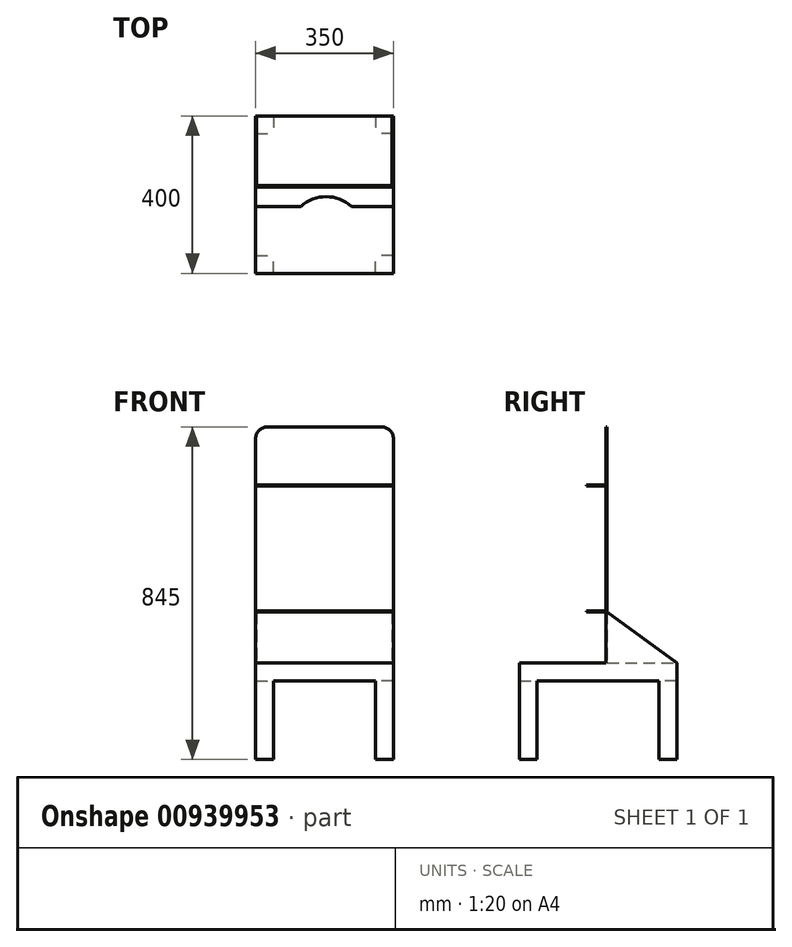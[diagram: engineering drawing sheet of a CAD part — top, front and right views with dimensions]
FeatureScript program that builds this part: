
annotation { "Feature Type Name" : "Feature", "Feature Type Description" : "" }
export const myFeature = defineFeature(function(context is Context, id is Id, definition is map)
    precondition{}
    {
        {
            var Q0;
            Q0=qCreatedBy(makeId("Top.planeOp"),FACE);
            var sketch = newSketch(context, id + "F0", { "sketchPlane" : qUnion([Q0])});
            skLineSegment(sketch, "E0.bottom", {"start": v(175, -200) * mm, "end": v(-175, -200) * mm});
            skLineSegment(sketch, "E0.top", {"start": v(175, 200) * mm, "end": v(-175, 200) * mm});
            skLineSegment(sketch, "E0.left", {"start": v(175, -200) * mm, "end": v(175, 200) * mm});
            skLineSegment(sketch, "E0.right", {"start": v(-175, -200) * mm, "end": v(-175, 200) * mm});
            skPoint(sketch, "E0.middle", {"position": v(0, 0) * mm});
            skSolve(sketch);
        }
        {
            var Q0;
            Q0=makeQuery(id+"F0.imprint","IMPRINT",FACE,{"disambiguationData":[TD([[makeQuery(id+"F0.imprint","IMPRINT",EDGE,{"derivedFrom":sQuery(id+"F0.wireOp",EDGE,"E0.bottom")}),-1.0]])]});
            extrude(context, id + "F1", {"entities" : qUnion([Q0]), "depth" : 45 * mm, "offsetDistance" : 25 * mm});
        }
        {
            var Q0;
            Q0=makeQuery(id+"F1.opExtrude","CAP_FACE",FACE,{"disambiguationData":[OSD([sQuery(id+"F0.wireOp",EDGE,"E0.bottom"),sQuery(id+"F0.wireOp",EDGE,"E0.top"),sQuery(id+"F0.wireOp",EDGE,"E0.left"),sQuery(id+"F0.wireOp",EDGE,"E0.right")])],"isStart":true});
            var sketch = newSketch(context, id + "F2", { "sketchPlane" : qUnion([Q0])});
            skLineSegment(sketch, "E1.bottom", {"start": v(-175, 200) * mm, "end": v(-130, 200) * mm});
            skLineSegment(sketch, "E1.top", {"start": v(-175, 155) * mm, "end": v(-130, 155) * mm});
            skLineSegment(sketch, "E1.left", {"start": v(-175, 200) * mm, "end": v(-175, 155) * mm});
            skLineSegment(sketch, "E1.right", {"start": v(-130, 200) * mm, "end": v(-130, 155) * mm});
            skLineSegment(sketch, "E2.bottom", {"start": v(175, 200) * mm, "end": v(130, 200) * mm});
            skLineSegment(sketch, "E2.top", {"start": v(175, 155) * mm, "end": v(130, 155) * mm});
            skLineSegment(sketch, "E2.left", {"start": v(175, 200) * mm, "end": v(175, 155) * mm});
            skLineSegment(sketch, "E2.right", {"start": v(130, 200) * mm, "end": v(130, 155) * mm});
            skLineSegment(sketch, "E3.bottom", {"start": v(-175, -200) * mm, "end": v(-130, -200) * mm});
            skLineSegment(sketch, "E3.top", {"start": v(-175, -155) * mm, "end": v(-130, -155) * mm});
            skLineSegment(sketch, "E3.left", {"start": v(-175, -200) * mm, "end": v(-175, -155) * mm});
            skLineSegment(sketch, "E3.right", {"start": v(-130, -200) * mm, "end": v(-130, -155) * mm});
            skLineSegment(sketch, "E4.bottom", {"start": v(175, -200) * mm, "end": v(130, -200) * mm});
            skLineSegment(sketch, "E4.top", {"start": v(175, -155) * mm, "end": v(130, -155) * mm});
            skLineSegment(sketch, "E4.left", {"start": v(175, -200) * mm, "end": v(175, -155) * mm});
            skLineSegment(sketch, "E4.right", {"start": v(130, -200) * mm, "end": v(130, -155) * mm});
            skSolve(sketch);
        }
        {
            var Q0;
            Q0=makeQuery(id+"F2.imprint","IMPRINT",FACE,{"disambiguationData":[TD([[makeQuery(id+"F2.imprint","IMPRINT",EDGE,{"derivedFrom":sQuery(id+"F2.wireOp",EDGE,"E1.bottom")}),1.0]])]});
            var Q1;
            Q1=makeQuery(id+"F2.imprint","IMPRINT",FACE,{"disambiguationData":[TD([[makeQuery(id+"F2.imprint","IMPRINT",EDGE,{"derivedFrom":sQuery(id+"F2.wireOp",EDGE,"E2.bottom")}),1.0]])]});
            var Q2;
            Q2=makeQuery(id+"F2.imprint","IMPRINT",FACE,{"disambiguationData":[TD([[makeQuery(id+"F2.imprint","IMPRINT",EDGE,{"derivedFrom":sQuery(id+"F2.wireOp",EDGE,"E3.bottom")}),-1.0]])]});
            var Q3;
            Q3=makeQuery(id+"F2.imprint","IMPRINT",FACE,{"disambiguationData":[TD([[makeQuery(id+"F2.imprint","IMPRINT",EDGE,{"derivedFrom":sQuery(id+"F2.wireOp",EDGE,"E4.bottom")}),-1.0]])]});
            extrude(context, id + "F3", {"entities" : qUnion([Q0, Q1, Q2, Q3]), "operationType" : NewBodyOperationType.ADD, "depth" : 200 * mm, "offsetDistance" : 25 * mm});
        }
        {
            var Q0;
            Q0=makeQuery(id+"F1.opExtrude","CAP_FACE",FACE,{"disambiguationData":[OSD([sQuery(id+"F0.wireOp",EDGE,"E0.bottom"),sQuery(id+"F0.wireOp",EDGE,"E0.top"),sQuery(id+"F0.wireOp",EDGE,"E0.left"),sQuery(id+"F0.wireOp",EDGE,"E0.right")])],"isStart":false});
            var sketch = newSketch(context, id + "F4", { "sketchPlane" : qUnion([Q0])});
            skPoint(sketch, "E5", {"position": v(-175, 20) * mm});
            skLineSegment(sketch, "E6.bottom", {"start": v(-175, 20) * mm, "end": v(175, 20) * mm});
            skLineSegment(sketch, "E6.top", {"start": v(-175, 23) * mm, "end": v(175, 23) * mm});
            skLineSegment(sketch, "E6.left", {"start": v(-175, 20) * mm, "end": v(-175, 23) * mm});
            skLineSegment(sketch, "E6.right", {"start": v(175, 20) * mm, "end": v(175, 23) * mm});
            skSolve(sketch);
        }
        {
            var Q0;
            Q0=makeQuery(id+"F4.imprint","IMPRINT",FACE,{"disambiguationData":[TD([[makeQuery(id+"F4.imprint","IMPRINT",EDGE,{"derivedFrom":sQuery(id+"F4.wireOp",EDGE,"E6.bottom")}),1.0]])]});
            extrude(context, id + "F5", {"entities" : qUnion([Q0]), "operationType" : NewBodyOperationType.ADD, "depth" : 600 * mm, "offsetDistance" : 25 * mm});
        }
        {
            var Q0;
            Q0=makeQuery(id+"F5.opExtrude","CAP_EDGE",EDGE,{"disambiguationData":[OSD([sQuery(id+"F4.wireOp",EDGE,"E6.left")])],"isStart":false});
            var Q1;
            Q1=makeQuery(id+"F5.opExtrude","CAP_EDGE",EDGE,{"disambiguationData":[OSD([sQuery(id+"F4.wireOp",EDGE,"E6.right")])],"isStart":false});
            fillet(context, id + "F6", {"entities" : qUnion([Q0, Q1]), "radius" : 30 * mm, "tangentPropagation" : true, "allowEdgeOverflow" : false});
        }
        {
            var Q0;
            Q0=makeQuery(id+"F5.boolean.opBoolean","MERGE",FACE,{"derivedFrom":[makeQuery(id+"F3.boolean.opBoolean","MERGE",FACE,{"derivedFrom":[makeQuery(id+"F1.opExtrude","SWEPT_FACE",FACE,{"disambiguationData":[OSD([sQuery(id+"F0.wireOp",EDGE,"E0.left")])]}),makeQuery(id+"F3.opExtrude","SWEPT_FACE",FACE,{"disambiguationData":[OSD([sQuery(id+"F2.wireOp",EDGE,"E2.left")])]}),makeQuery(id+"F3.opExtrude","SWEPT_FACE",FACE,{"disambiguationData":[OSD([sQuery(id+"F2.wireOp",EDGE,"E4.left")])]})]}),makeQuery(id+"F5.opExtrude","SWEPT_FACE",FACE,{"disambiguationData":[OSD([sQuery(id+"F4.wireOp",EDGE,"E6.right")])]})]});
            var sketch = newSketch(context, id + "F7", { "sketchPlane" : qUnion([Q0])});
            skLineSegment(sketch, "E7", {"start": v(200, 45) * mm, "end": v(23, 45) * mm});
            skLineSegment(sketch, "E8", {"start": v(23, 45) * mm, "end": v(23, 175) * mm});
            skLineSegment(sketch, "E9", {"start": v(23, 175) * mm, "end": v(200, 45) * mm});
            skSolve(sketch);
        }
        {
            var Q0;
            Q0=makeQuery(id+"F7.imprint","IMPRINT",FACE,{"disambiguationData":[TD([[makeQuery(id+"F7.imprint","IMPRINT",EDGE,{"derivedFrom":sQuery(id+"F7.wireOp",EDGE,"E7")}),1.0]])]});
            extrude(context, id + "F8", {"entities" : qUnion([Q0]), "operationType" : NewBodyOperationType.ADD, "oppositeDirection" : true, "depth" : 3 * mm, "offsetDistance" : 25 * mm});
        }
        {
            var Q0;
            Q0=makeQuery(id+"F5.boolean.opBoolean","MERGE",FACE,{"derivedFrom":[makeQuery(id+"F3.boolean.opBoolean","MERGE",FACE,{"derivedFrom":[makeQuery(id+"F1.opExtrude","SWEPT_FACE",FACE,{"disambiguationData":[OSD([sQuery(id+"F0.wireOp",EDGE,"E0.right")])]}),makeQuery(id+"F3.opExtrude","SWEPT_FACE",FACE,{"disambiguationData":[OSD([sQuery(id+"F2.wireOp",EDGE,"E1.left")])]}),makeQuery(id+"F3.opExtrude","SWEPT_FACE",FACE,{"disambiguationData":[OSD([sQuery(id+"F2.wireOp",EDGE,"E3.left")])]})]}),makeQuery(id+"F5.opExtrude","SWEPT_FACE",FACE,{"disambiguationData":[OSD([sQuery(id+"F4.wireOp",EDGE,"E6.left")])]})]});
            var sketch = newSketch(context, id + "F9", { "sketchPlane" : qUnion([Q0])});
            skLineSegment(sketch, "E10", {"start": v(-200, 45) * mm, "end": v(-23, 45) * mm});
            skLineSegment(sketch, "E11", {"start": v(-23, 45) * mm, "end": v(-23, 175) * mm});
            skLineSegment(sketch, "E12", {"start": v(-23, 175) * mm, "end": v(-200, 45) * mm});
            skSolve(sketch);
        }
        {
            var Q0;
            Q0=makeQuery(id+"F9.imprint","IMPRINT",FACE,{"disambiguationData":[TD([[makeQuery(id+"F9.imprint","IMPRINT",EDGE,{"derivedFrom":sQuery(id+"F9.wireOp",EDGE,"E10")}),-1.0]])]});
            extrude(context, id + "F10", {"entities" : qUnion([Q0]), "operationType" : NewBodyOperationType.ADD, "oppositeDirection" : true, "depth" : 3 * mm, "offsetDistance" : 25 * mm});
        }
        {
            var Q0;
            Q0=makeQuery(id+"F5.opExtrude","SWEPT_FACE",FACE,{"disambiguationData":[OSD([sQuery(id+"F4.wireOp",EDGE,"E6.bottom")])]});
            var sketch = newSketch(context, id + "F11", { "sketchPlane" : qUnion([Q0])});
            skPoint(sketch, "E13", {"position": v(-175, 495) * mm});
            skPoint(sketch, "E14", {"position": v(175, 495) * mm});
            skPoint(sketch, "E15", {"position": v(-175, 175) * mm});
            skPoint(sketch, "E16", {"position": v(175, 175) * mm});
            skLineSegment(sketch, "E17.bottom", {"start": v(-175, 495) * mm, "end": v(175, 495) * mm});
            skLineSegment(sketch, "E17.top", {"start": v(-175, 498) * mm, "end": v(175, 498) * mm});
            skLineSegment(sketch, "E17.left", {"start": v(-175, 495) * mm, "end": v(-175, 498) * mm});
            skLineSegment(sketch, "E17.right", {"start": v(175, 495) * mm, "end": v(175, 498) * mm});
            skLineSegment(sketch, "E18.bottom", {"start": v(-175, 175) * mm, "end": v(175, 175) * mm});
            skLineSegment(sketch, "E18.top", {"start": v(-175, 178) * mm, "end": v(175, 178) * mm});
            skLineSegment(sketch, "E18.left", {"start": v(-175, 175) * mm, "end": v(-175, 178) * mm});
            skLineSegment(sketch, "E18.right", {"start": v(175, 175) * mm, "end": v(175, 178) * mm});
            skSolve(sketch);
        }
        {
            var Q0;
            Q0=makeQuery(id+"F11.imprint","IMPRINT",FACE,{"disambiguationData":[TD([[makeQuery(id+"F11.imprint","IMPRINT",EDGE,{"derivedFrom":sQuery(id+"F11.wireOp",EDGE,"E18.bottom")}),1.0]])]});
            var Q1;
            Q1=makeQuery(id+"F11.imprint","IMPRINT",FACE,{"disambiguationData":[TD([[makeQuery(id+"F11.imprint","IMPRINT",EDGE,{"derivedFrom":sQuery(id+"F11.wireOp",EDGE,"E17.bottom")}),1.0]])]});
            extrude(context, id + "F12", {"entities" : qUnion([Q0, Q1]), "operationType" : NewBodyOperationType.ADD, "depth" : 50 * mm, "offsetDistance" : 25 * mm});
        }
        {
            var Q0;
            Q0=makeQuery(id+"F12.opExtrude","SWEPT_FACE",FACE,{"disambiguationData":[OSD([sQuery(id+"F11.wireOp",EDGE,"E17.top")])]});
            var sketch = newSketch(context, id + "F13", { "sketchPlane" : qUnion([Q0])});
            skPoint(sketch, "E19", {"position": v(0, 0) * mm});
            skPoint(sketch, "E20", {"position": v(4.08, -100) * mm});
            skCircle(sketch, "E21", {"center": v(4.08, -100) * mm, "radius": 95 * mm});
            skSolve(sketch);
        }
        {
            var Q0;
            {var subQ0=sQuery(id+"F13.wireOp",EDGE,"E21");var subQ1=makeQuery(id+"F12.opExtrude","CAP_EDGE",EDGE,{"disambiguationData":[OSD([sQuery(id+"F11.wireOp",EDGE,"E17.top")])],"isStart":false});var subQ2=makeQuery(id+"F13.imprint","INTERSECT",VERTEX,{"disambiguationData":[OD(0.0)],"derivedFrom":[subQ1,subQ0]});Q0=makeQuery(id+"F13.imprint","IMPRINT",FACE,{"disambiguationData":[TD([[makeQuery(id+"F13.imprint","IMPRINT",EDGE,{"disambiguationData":[TD([[subQ2,-1.0]])],"derivedFrom":subQ0}),1.0]])]});}
            var Q1;
            {var subQ0=sQuery(id+"F13.wireOp",EDGE,"E21");var subQ1=makeQuery(id+"F12.opExtrude","CAP_EDGE",EDGE,{"disambiguationData":[OSD([sQuery(id+"F11.wireOp",EDGE,"E17.top")])],"isStart":false});var subQ2=makeQuery(id+"F13.imprint","INTERSECT",VERTEX,{"disambiguationData":[OD(0.0)],"derivedFrom":[subQ1,subQ0]});Q1=makeQuery(id+"F13.imprint","IMPRINT",FACE,{"disambiguationData":[TD([[makeQuery(id+"F13.imprint","IMPRINT",EDGE,{"disambiguationData":[TD([[subQ2,1.0]])],"derivedFrom":subQ0}),1.0]])]});}
            extrude(context, id + "F14", {"entities" : qUnion([Q0, Q1]), "operationType" : NewBodyOperationType.REMOVE, "oppositeDirection" : true, "depth" : 350 * mm, "offsetDistance" : 25 * mm});
        }
    });
